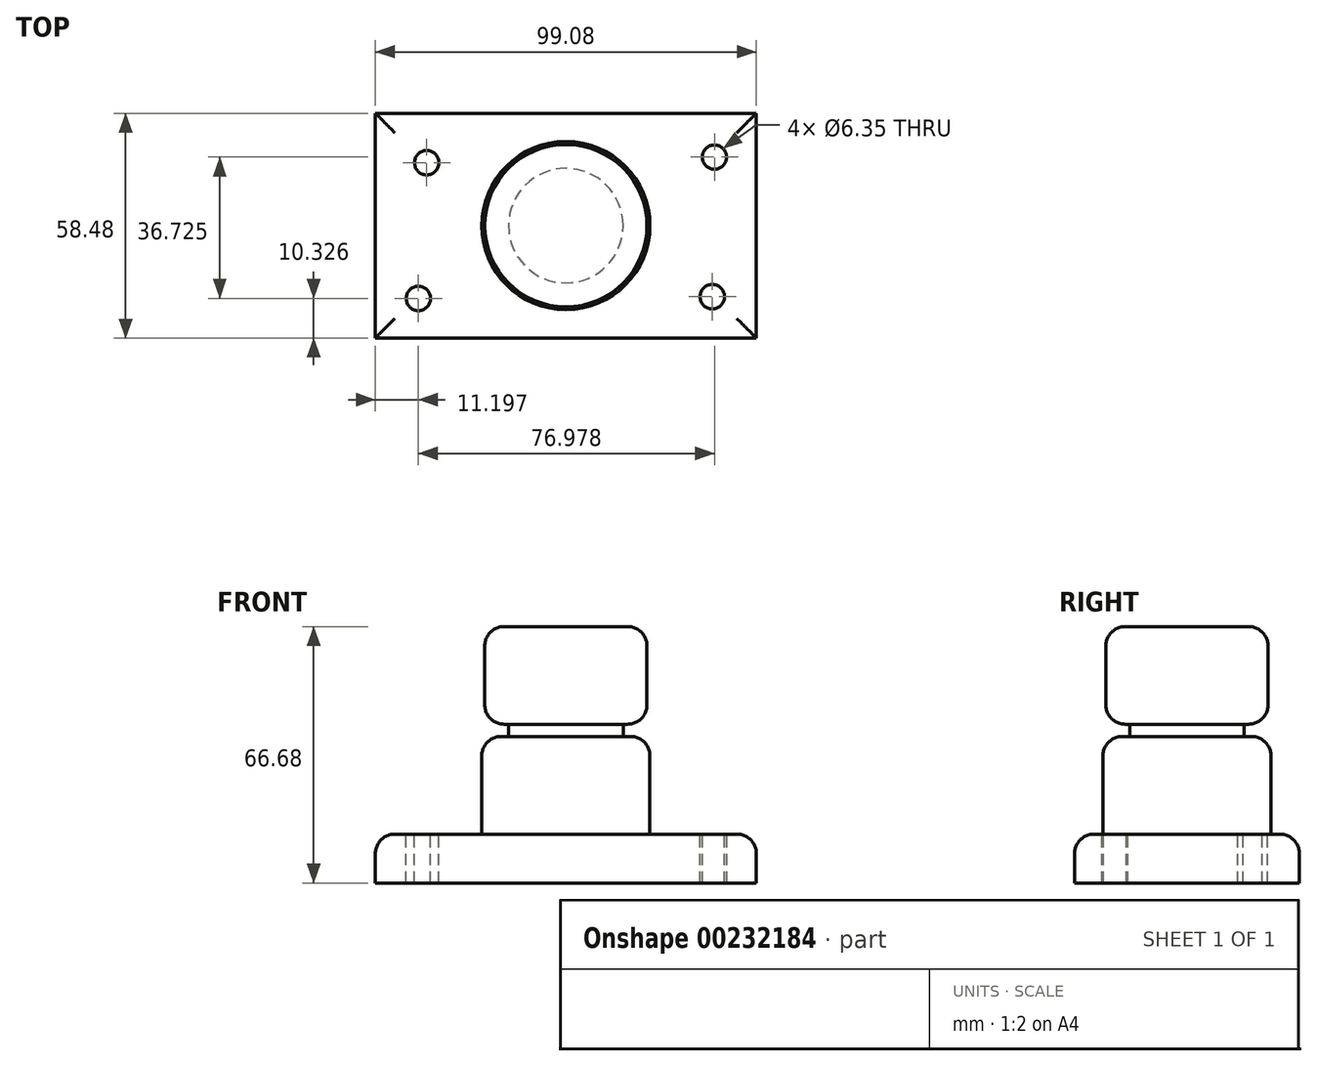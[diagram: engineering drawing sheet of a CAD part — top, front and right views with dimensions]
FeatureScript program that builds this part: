
annotation { "Feature Type Name" : "Feature", "Feature Type Description" : "" }
export const myFeature = defineFeature(function(context is Context, id is Id, definition is map)
    precondition{}
    {
        {
            var Q0;
            Q0=qCreatedBy(makeId("Top.planeOp"),FACE);
            var sketch = newSketch(context, id + "F0", { "sketchPlane" : qUnion([Q0])});
            skLineSegment(sketch, "E0.bottom", {"start": v(49.54, -29.24) * mm, "end": v(-49.54, -29.24) * mm});
            skLineSegment(sketch, "E0.top", {"start": v(49.54, 29.24) * mm, "end": v(-49.54, 29.24) * mm});
            skLineSegment(sketch, "E0.left", {"start": v(49.54, -29.24) * mm, "end": v(49.54, 29.24) * mm});
            skLineSegment(sketch, "E0.right", {"start": v(-49.54, -29.24) * mm, "end": v(-49.54, 29.24) * mm});
            skPoint(sketch, "E0.middle", {"position": v(0, 0) * mm});
            skCircle(sketch, "E1", {"center": v(0, 0) * mm, "radius": 16.37 * mm});
            skPoint(sketch, "E2", {"position": v(-38.82, -18.75) * mm});
            skPoint(sketch, "E3", {"position": v(37.44, -18.34) * mm});
            skPoint(sketch, "E4", {"position": v(37.44, 19.99) * mm});
            skPoint(sketch, "E5", {"position": v(-38.82, 19.99) * mm});
            skSolve(sketch);
        }
        {
            var Q0;
            Q0=makeQuery(id+"F0.imprint","IMPRINT",FACE,{"disambiguationData":[TD([[makeQuery(id+"F0.imprint","IMPRINT",EDGE,{"derivedFrom":sQuery(id+"F0.wireOp",EDGE,"E1")}),1.0]])]});
            var Q1;
            Q1=makeQuery(id+"F0.imprint","IMPRINT",FACE,{"disambiguationData":[TD([[makeQuery(id+"F0.imprint","IMPRINT",EDGE,{"derivedFrom":sQuery(id+"F0.wireOp",EDGE,"E0.bottom")}),-1.0]])]});
            extrude(context, id + "F1", {"entities" : qUnion([Q0, Q1]), "depth" : 12.7 * mm});
        }
        {
            var Q0;
            Q0=makeQuery(id+"F1.opExtrude","CAP_FACE",FACE,{"disambiguationData":[OSD([sQuery(id+"F0.wireOp",EDGE,"E0.bottom"),sQuery(id+"F0.wireOp",EDGE,"E0.top"),sQuery(id+"F0.wireOp",EDGE,"E0.left"),sQuery(id+"F0.wireOp",EDGE,"E0.right")])],"isStart":false});
            var sketch = newSketch(context, id + "F2", { "sketchPlane" : qUnion([Q0])});
            skCircle(sketch, "E6", {"center": v(0, 0) * mm, "radius": 21.86 * mm});
            skSolve(sketch);
        }
        {
            var Q0;
            Q0=makeQuery(id+"F2.imprint","IMPRINT",FACE,{"disambiguationData":[TD([[makeQuery(id+"F2.imprint","IMPRINT",EDGE,{"derivedFrom":sQuery(id+"F2.wireOp",EDGE,"E6")}),1.0]])]});
            extrude(context, id + "F3", {"entities" : qUnion([Q0]), "operationType" : NewBodyOperationType.ADD, "depth" : 25.4 * mm});
        }
        {
            var Q0;
            Q0=makeQuery(id+"F1.opExtrude","CAP_EDGE",EDGE,{"disambiguationData":[OSD([sQuery(id+"F0.wireOp",EDGE,"E0.top")])],"isStart":false});
            var Q1;
            Q1=makeQuery(id+"F1.opExtrude","CAP_EDGE",EDGE,{"disambiguationData":[OSD([sQuery(id+"F0.wireOp",EDGE,"E0.left")])],"isStart":false});
            var Q2;
            Q2=makeQuery(id+"F1.opExtrude","CAP_EDGE",EDGE,{"disambiguationData":[OSD([sQuery(id+"F0.wireOp",EDGE,"E0.bottom")])],"isStart":false});
            var Q3;
            Q3=makeQuery(id+"F1.opExtrude","CAP_EDGE",EDGE,{"disambiguationData":[OSD([sQuery(id+"F0.wireOp",EDGE,"E0.right")])],"isStart":false});
            fillet(context, id + "F4", {"entities" : qUnion([Q0, Q1, Q2, Q3]), "radius" : 5.08 * mm, "tangentPropagation" : true, "allowEdgeOverflow" : false});
        }
        {
            var Q0;
            Q0=makeQuery(id+"F3.opExtrude","CAP_FACE",FACE,{"disambiguationData":[OSD([sQuery(id+"F2.wireOp",EDGE,"E6")])],"isStart":false});
            var sketch = newSketch(context, id + "F5", { "sketchPlane" : qUnion([Q0])});
            skCircle(sketch, "E7", {"center": v(0, 0) * mm, "radius": 14.9 * mm});
            skSolve(sketch);
        }
        {
            var Q0;
            Q0=makeQuery(id+"F5.imprint","IMPRINT",FACE,{"disambiguationData":[TD([[makeQuery(id+"F5.imprint","IMPRINT",EDGE,{"derivedFrom":sQuery(id+"F5.wireOp",EDGE,"E7")}),1.0]])]});
            extrude(context, id + "F6", {"entities" : qUnion([Q0]), "operationType" : NewBodyOperationType.ADD, "depth" : 3.17 * mm});
        }
        {
            var Q0;
            Q0=makeQuery(id+"F6.opExtrude","CAP_FACE",FACE,{"disambiguationData":[OSD([sQuery(id+"F5.wireOp",EDGE,"E7")])],"isStart":false});
            var sketch = newSketch(context, id + "F7", { "sketchPlane" : qUnion([Q0])});
            skCircle(sketch, "E8", {"center": v(0, 0) * mm, "radius": 21.1 * mm});
            skSolve(sketch);
        }
        {
            var Q0;
            Q0=makeQuery(id+"F7.imprint","IMPRINT",FACE,{"disambiguationData":[TD([[makeQuery(id+"F7.imprint","IMPRINT",EDGE,{"derivedFrom":sQuery(id+"F7.wireOp",EDGE,"E8")}),1.0]])]});
            var Q1;
            Q1=makeQuery(id+"F7.imprint","IMPRINT",FACE,{"disambiguationData":[TD([[makeQuery(id+"F7.imprint","IMPRINT",EDGE,{"derivedFrom":makeQuery(id+"F6.opExtrude","CAP_EDGE",EDGE,{"disambiguationData":[OSD([sQuery(id+"F5.wireOp",EDGE,"E7")])],"isStart":false})}),1.0]])]});
            extrude(context, id + "F8", {"entities" : qUnion([Q0, Q1]), "operationType" : NewBodyOperationType.ADD, "depth" : 25.4 * mm});
        }
        {
            var Q0;
            Q0=makeQuery(id+"F8.opExtrude","CAP_EDGE",EDGE,{"disambiguationData":[OSD([sQuery(id+"F7.wireOp",EDGE,"E8")])],"isStart":true});
            var Q1;
            Q1=makeQuery(id+"F3.opExtrude","CAP_EDGE",EDGE,{"disambiguationData":[OSD([sQuery(id+"F2.wireOp",EDGE,"E6")])],"isStart":false});
            fillet(context, id + "F9", {"entities" : qUnion([Q0, Q1]), "radius" : 5.08 * mm, "tangentPropagation" : true, "allowEdgeOverflow" : false});
        }
        {
            var Q0;
            Q0=makeQuery(id+"F1.opExtrude","CAP_FACE",FACE,{"disambiguationData":[OSD([sQuery(id+"F0.wireOp",EDGE,"E0.bottom"),sQuery(id+"F0.wireOp",EDGE,"E0.top"),sQuery(id+"F0.wireOp",EDGE,"E0.left"),sQuery(id+"F0.wireOp",EDGE,"E0.right")])],"isStart":false});
            var sketch = newSketch(context, id + "F10", { "sketchPlane" : qUnion([Q0])});
            skPoint(sketch, "E9", {"position": v(38.63, 17.81) * mm});
            skPoint(sketch, "E10", {"position": v(38.07, -18.48) * mm});
            skPoint(sketch, "E11", {"position": v(-36.18, 16.37) * mm});
            skPoint(sketch, "E12", {"position": v(-38.34, -18.91) * mm});
            skSolve(sketch);
        }
        {
            var Q0;
            Q0=sQuery(id+"F10.wireOp",VERTEX,"E9");
            var Q1;
            Q1=sQuery(id+"F10.wireOp",VERTEX,"E10");
            var Q2;
            Q2=sQuery(id+"F10.wireOp",VERTEX,"E11");
            var Q3;
            Q3=sQuery(id+"F10.wireOp",VERTEX,"E12");
            var Q4;
            Q4=makeQuery(id+"F1.opExtrude","SWEPT_BODY",BODY,{"disambiguationData":[OSD([sQuery(id+"F0.wireOp",EDGE,"E0.bottom"),sQuery(id+"F0.wireOp",EDGE,"E0.top"),sQuery(id+"F0.wireOp",EDGE,"E0.left"),sQuery(id+"F0.wireOp",EDGE,"E0.right")])]});
            hole(context, id + "F11", {"style" : HoleStyle.SIMPLE, "endStyle" : HoleEndStyle.THROUGH, "holeDiameter" : 6.35 * mm, "locations" : qUnion([Q0, Q1, Q2, Q3]), "scope" : qUnion([Q4]), "isTappedThrough" : true});
        }
        {
            var Q0;
            Q0=makeQuery(id+"F8.opExtrude","CAP_EDGE",EDGE,{"disambiguationData":[OSD([sQuery(id+"F7.wireOp",EDGE,"E8")])],"isStart":false});
            fillet(context, id + "F12", {"entities" : qUnion([Q0]), "radius" : 5.08 * mm, "tangentPropagation" : true, "allowEdgeOverflow" : false});
        }
    });
